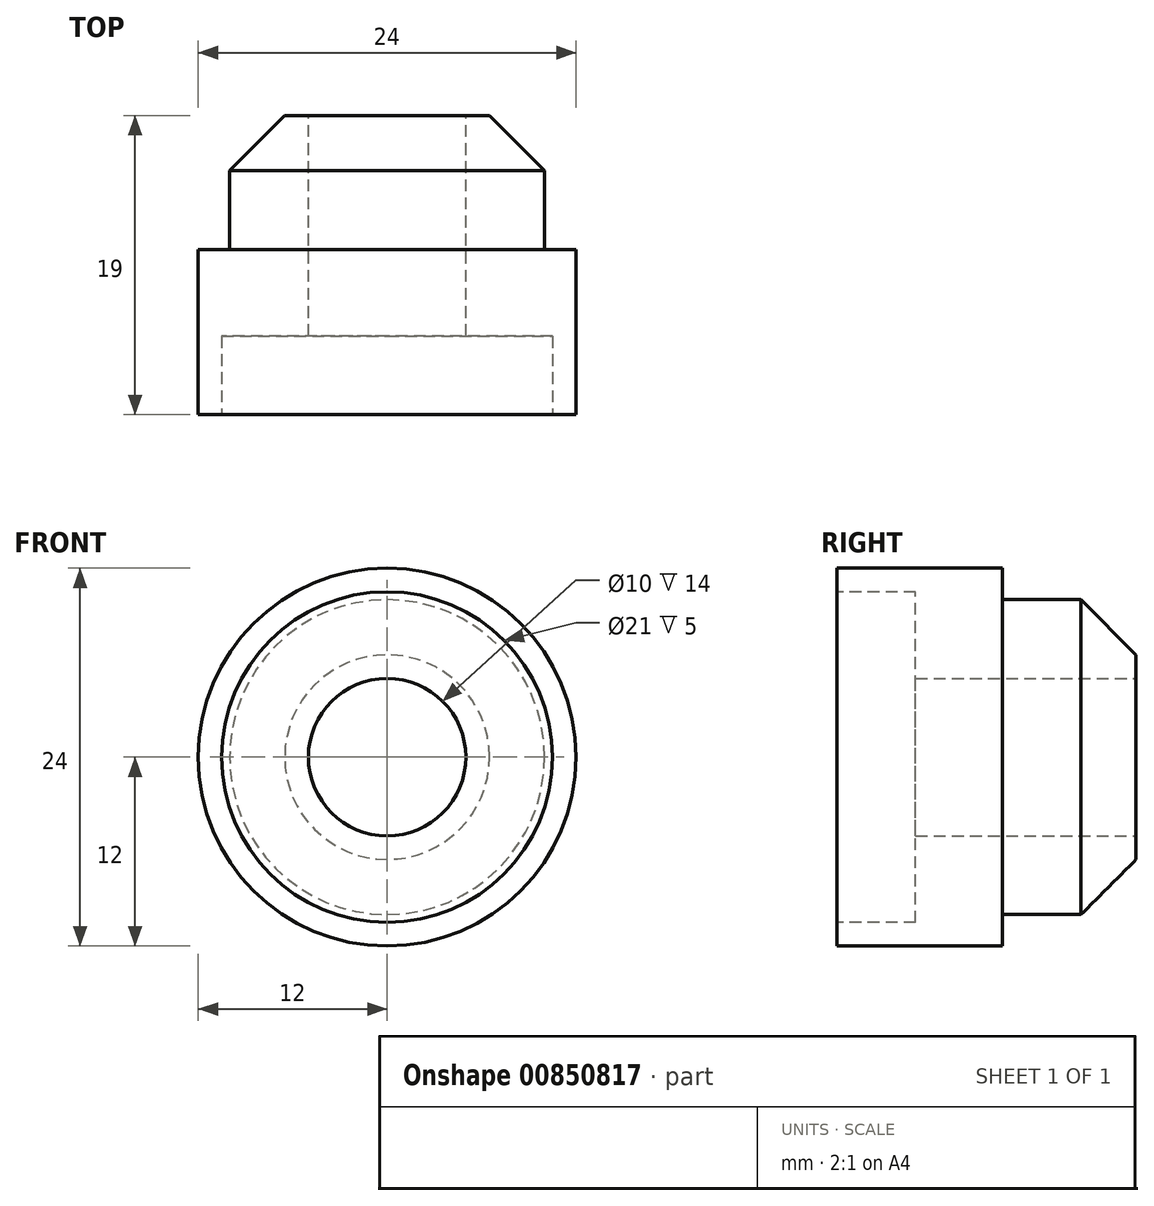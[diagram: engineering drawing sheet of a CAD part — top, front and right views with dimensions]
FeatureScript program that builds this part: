
annotation { "Feature Type Name" : "Feature", "Feature Type Description" : "" }
export const myFeature = defineFeature(function(context is Context, id is Id, definition is map)
    precondition{}
    {
        {
            var Q0;
            Q0=qCreatedBy(makeId("Front.planeOp"),FACE);
            var sketch = newSketch(context, id + "F0", { "sketchPlane" : qUnion([Q0])});
            skCircle(sketch, "E0", {"center": v(0, 0) * mm, "radius": 12 * mm});
            skSolve(sketch);
        }
        {
            var Q0;
            Q0=qSketchRegion(id+"F0",true);
            extrude(context, id + "F1", {"entities" : qUnion([Q0]), "oppositeDirection" : true, "depth" : 19 * mm, "offsetDistance" : 25 * mm});
        }
        {
            var Q0;
            Q0=qCreatedBy(makeId("Front.planeOp"),FACE);
            cPlane(context, id + "F2", {"entities" : qUnion([Q0]), "cplaneType" : CPlaneType.OFFSET, "offset" : 10.5 * mm, "oppositeDirection" : true, "width" : 150 * mm, "height" : 150 * mm});
        }
        {
            var Q0;
            Q0=qCreatedBy(id+"F2.planeOp",FACE);
            var sketch = newSketch(context, id + "F3", { "sketchPlane" : qUnion([Q0])});
            skCircle(sketch, "E1", {"center": v(0, 0) * mm, "radius": 12 * mm});
            skCircle(sketch, "E2", {"center": v(0, 0) * mm, "radius": 10 * mm});
            skSolve(sketch);
        }
        {
            var Q0;
            Q0=qSketchRegion(id+"F3",true);
            extrude(context, id + "F4", {"entities" : qUnion([Q0]), "operationType" : NewBodyOperationType.REMOVE, "oppositeDirection" : true, "depth" : 13 * mm, "offsetDistance" : 25 * mm});
        }
        {
            var Q0;
            Q0=makeQuery(id+"F1.opExtrude","CAP_FACE",FACE,{"disambiguationData":[OSD([sQuery(id+"F0.wireOp",EDGE,"E0")])],"isStart":false});
            cPlane(context, id + "F5", {"entities" : qUnion([Q0]), "cplaneType" : CPlaneType.OFFSET, "offset" : 0 * mm, "width" : 150 * mm, "height" : 150 * mm});
        }
        {
            var Q0;
            Q0=qCreatedBy(id+"F5.planeOp",FACE);
            var sketch = newSketch(context, id + "F6", { "sketchPlane" : qUnion([Q0])});
            skCircle(sketch, "E3", {"center": v(0, 0) * mm, "radius": 5 * mm});
            skSolve(sketch);
        }
        {
            var Q0;
            Q0=makeQuery(id+"F6.imprint","IMPRINT",FACE,{"disambiguationData":[TD([[makeQuery(id+"F6.imprint","IMPRINT",EDGE,{"derivedFrom":sQuery(id+"F6.wireOp",EDGE,"E3")}),1.0]])]});
            extrude(context, id + "F7", {"entities" : qUnion([Q0]), "operationType" : NewBodyOperationType.REMOVE, "oppositeDirection" : true, "depth" : 25 * mm, "offsetDistance" : 25 * mm});
        }
        {
            var Q0;
            Q0=qCreatedBy(makeId("Front.planeOp"),FACE);
            var sketch = newSketch(context, id + "F8", { "sketchPlane" : qUnion([Q0])});
            skCircle(sketch, "E4", {"center": v(0, 0) * mm, "radius": 12 * mm});
            skCircle(sketch, "E5", {"center": v(0, 0) * mm, "radius": 10.5 * mm});
            skSolve(sketch);
        }
        {
            var Q0;
            Q0=makeQuery(id+"F8.imprint","IMPRINT",FACE,{"disambiguationData":[TD([[makeQuery(id+"F8.imprint","IMPRINT",EDGE,{"derivedFrom":sQuery(id+"F8.wireOp",EDGE,"E5")}),1.0]])]});
            extrude(context, id + "F9", {"entities" : qUnion([Q0]), "operationType" : NewBodyOperationType.REMOVE, "oppositeDirection" : true, "depth" : 5 * mm, "offsetDistance" : 25 * mm});
        }
        {
            var Q0;
            Q0=makeQuery(id+"F4.boolean.opBoolean","INTERSECT",EDGE,{"derivedFrom":[makeQuery(id+"F1.opExtrude","CAP_FACE",FACE,{"disambiguationData":[OSD([sQuery(id+"F0.wireOp",EDGE,"E0")])],"isStart":false}),makeQuery(id+"F4.opExtrude","SWEPT_FACE",FACE,{"disambiguationData":[OSD([sQuery(id+"F3.wireOp",EDGE,"E2")])]})]});
            chamfer(context, id + "F10", {"entities" : qUnion([Q0]), "width" : 3.5 * mm, "tangentPropagation" : true});
        }
    });
